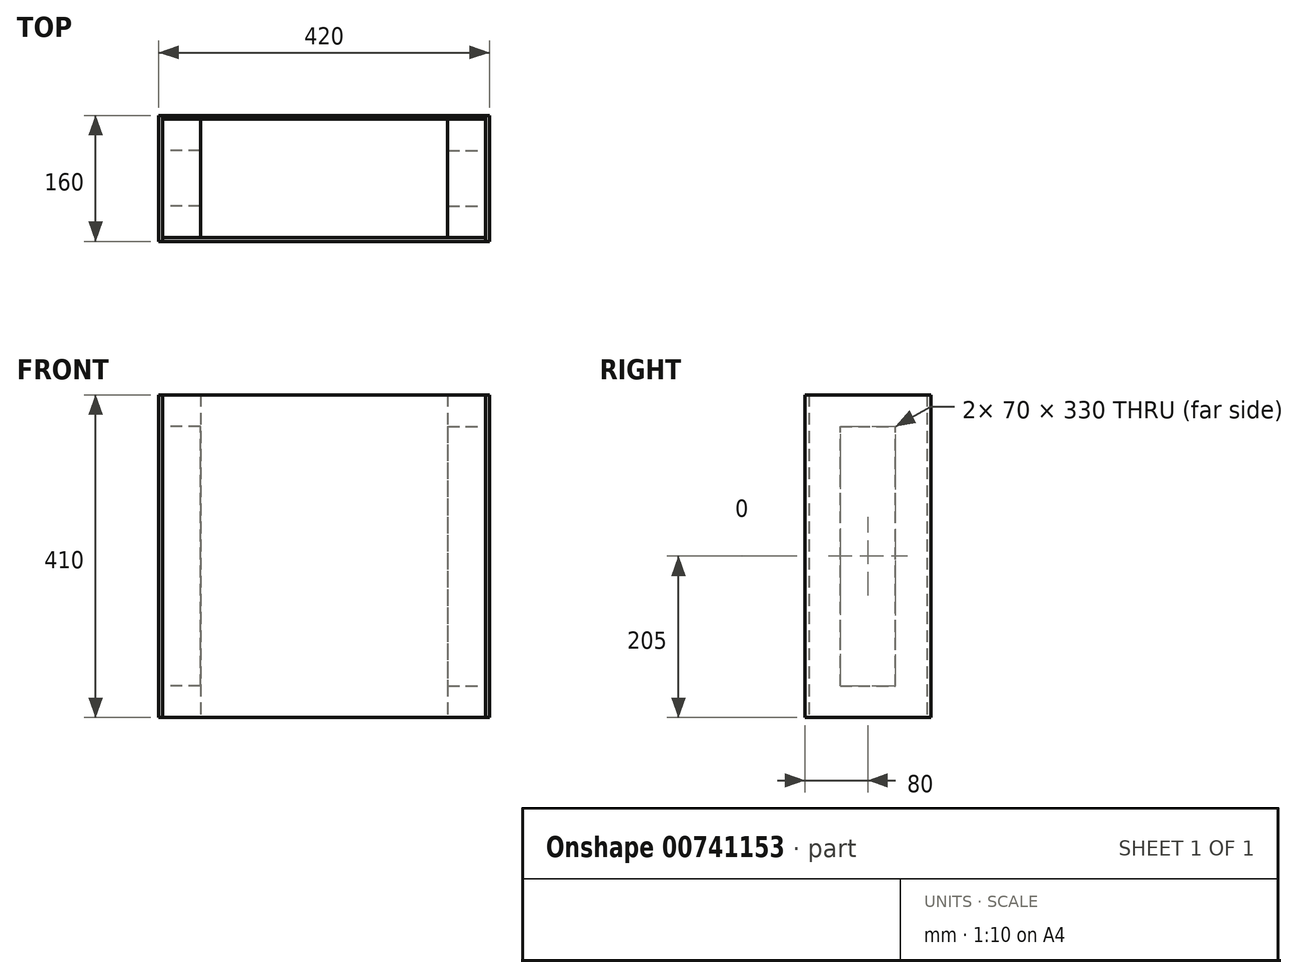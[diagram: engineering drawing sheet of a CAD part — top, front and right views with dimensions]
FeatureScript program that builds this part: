
annotation { "Feature Type Name" : "Feature", "Feature Type Description" : "" }
export const myFeature = defineFeature(function(context is Context, id is Id, definition is map)
    precondition{}
    {
        {
            var Q0;
            Q0=qCreatedBy(makeId("Front.planeOp"),FACE);
            var sketch = newSketch(context, id + "F0", { "sketchPlane" : qUnion([Q0])});
            skLineSegment(sketch, "E0.bottom", {"start": v(-205, 205) * mm, "end": v(205, 205) * mm});
            skLineSegment(sketch, "E0.top", {"start": v(-205, -205) * mm, "end": v(205, -205) * mm});
            skLineSegment(sketch, "E0.left", {"start": v(-205, 205) * mm, "end": v(-205, -205) * mm});
            skLineSegment(sketch, "E0.right", {"start": v(205, 205) * mm, "end": v(205, -205) * mm});
            skPoint(sketch, "E0.middle", {"position": v(0, 0) * mm});
            skSolve(sketch);
        }
        {
            var Q0;
            Q0 = qSketchRegion(id + "F0", true);
            extrude(context, id + "F1", {"entities" : qUnion([Q0]), "depth" : 5 * mm, "offsetDistance" : 25 * mm});
        }
        {
            var Q0;
            Q0=makeQuery(id+"F1.opExtrude","CAP_FACE",FACE,{"disambiguationData":[OSD([sQuery(id+"F0.wireOp",EDGE,"E0.bottom"),sQuery(id+"F0.wireOp",EDGE,"E0.top"),sQuery(id+"F0.wireOp",EDGE,"E0.left"),sQuery(id+"F0.wireOp",EDGE,"E0.right")])],"isStart":false});
            var sketch = newSketch(context, id + "F2", { "sketchPlane" : qUnion([Q0])});
            skLineSegment(sketch, "E1.0", {"start": v(-205, 205) * mm, "end": v(-205, -205) * mm});
            skLineSegment(sketch, "E2.0", {"start": v(205, 205) * mm, "end": v(205, -205) * mm});
            skLineSegment(sketch, "E3", {"start": v(0, 0) * mm, "end": v(0, 153.6) * mm, "construction": true});
            skLineSegment(sketch, "E4.bottom", {"start": v(-205, 205) * mm, "end": v(-157, 205) * mm});
            skLineSegment(sketch, "E4.top", {"start": v(-205, -205) * mm, "end": v(-157, -205) * mm});
            skLineSegment(sketch, "E4.right", {"start": v(-157, 205) * mm, "end": v(-157, -205) * mm});
            skLineSegment(sketch, "E5.MirrorCS", {"start": v(157, 205) * mm, "end": v(157, -205) * mm});
            skLineSegment(sketch, "E6.MirrorCS", {"start": v(205, 205) * mm, "end": v(157, 205) * mm});
            skLineSegment(sketch, "E7.MirrorCS", {"start": v(205, -205) * mm, "end": v(157, -205) * mm});
            skSolve(sketch);
        }
        {
            var Q0;
            Q0 = qSketchRegion(id + "F2", true);
            extrude(context, id + "F3", {"entities" : qUnion([Q0]), "depth" : 150 * mm, "offsetDistance" : 25 * mm});
        }
        {
            var Q0;
            Q0=makeQuery(id+"F3.opExtrude","CAP_FACE",FACE,{"disambiguationData":[OSD([sQuery(id+"F2.wireOp",EDGE,"E4.bottom"),sQuery(id+"F2.wireOp",EDGE,"E4.top"),sQuery(id+"F2.wireOp",EDGE,"E1.0"),sQuery(id+"F2.wireOp",EDGE,"E4.right")])],"isStart":false});
            var sketch = newSketch(context, id + "F4", { "sketchPlane" : qUnion([Q0])});
            skLineSegment(sketch, "E8.0", {"start": v(-205, 205) * mm, "end": v(-205, -205) * mm});
            skLineSegment(sketch, "E9.0", {"start": v(-205, 205) * mm, "end": v(205, 205) * mm});
            skLineSegment(sketch, "E10.0", {"start": v(205, 205) * mm, "end": v(205, -205) * mm});
            skLineSegment(sketch, "E11.0", {"start": v(-205, -205) * mm, "end": v(205, -205) * mm});
            skSolve(sketch);
        }
        {
            var Q0;
            Q0 = qSketchRegion(id + "F4", true);
            extrude(context, id + "F5", {"entities" : qUnion([Q0]), "depth" : 5 * mm, "offsetDistance" : 25 * mm});
        }
        {
            var Q0;
            Q0=makeQuery(id+"F3.opExtrude","SWEPT_FACE",FACE,{"disambiguationData":[OSD([sQuery(id+"F2.wireOp",EDGE,"E1.0")])]});
            var sketch = newSketch(context, id + "F6", { "sketchPlane" : qUnion([Q0])});
            skLineSegment(sketch, "E12.0", {"start": v(0, 205) * mm, "end": v(0, -205) * mm});
            skLineSegment(sketch, "E13.0", {"start": v(160, 205) * mm, "end": v(160, -205) * mm});
            skPoint(sketch, "E14.0.end.orphan", {"position": v(5, 205) * mm});
            skPoint(sketch, "E14.0.start.orphan", {"position": v(155, 205) * mm});
            skLineSegment(sketch, "E15", {"start": v(0, 205) * mm, "end": v(160, 205) * mm});
            skPoint(sketch, "E16.0.end.orphan", {"position": v(5, -205) * mm});
            skPoint(sketch, "E16.0.start.orphan", {"position": v(155, -205) * mm});
            skLineSegment(sketch, "E17", {"start": v(0, -205) * mm, "end": v(160, -205) * mm});
            skSolve(sketch);
        }
        {
            var Q0;
            Q0 = qSketchRegion(id + "F6", true);
            extrude(context, id + "F7", {"entities" : qUnion([Q0]), "depth" : 5 * mm, "offsetDistance" : 25 * mm});
        }
        {
            var Q0;
            Q0=makeQuery(id+"F3.opExtrude","SWEPT_FACE",FACE,{"disambiguationData":[OSD([sQuery(id+"F2.wireOp",EDGE,"E2.0")])]});
            var sketch = newSketch(context, id + "F8", { "sketchPlane" : qUnion([Q0])});
            skLineSegment(sketch, "E18.0", {"start": v(-160, 205) * mm, "end": v(-160, -205) * mm});
            skLineSegment(sketch, "E19.0", {"start": v(0, 205) * mm, "end": v(0, -205) * mm});
            skLineSegment(sketch, "E20", {"start": v(-160, 205) * mm, "end": v(0, 205) * mm});
            skLineSegment(sketch, "E21", {"start": v(-160, -205) * mm, "end": v(0, -205) * mm});
            skSolve(sketch);
        }
        {
            var Q0;
            Q0 = qSketchRegion(id + "F8", true);
            extrude(context, id + "F9", {"entities" : qUnion([Q0]), "depth" : 5 * mm, "offsetDistance" : 25 * mm});
        }
        {
            var Q0;
            Q0=makeQuery(id+"F3.opExtrude","SWEPT_FACE",FACE,{"disambiguationData":[OSD([sQuery(id+"F2.wireOp",EDGE,"E1.0")])]});
            var sketch = newSketch(context, id + "F10", { "sketchPlane" : qUnion([Q0])});
            skLineSegment(sketch, "E22.0", {"start": v(155, 205) * mm, "end": v(5, 205) * mm, "construction": true});
            skLineSegment(sketch, "E23.0", {"start": v(5, 205) * mm, "end": v(5, -205) * mm, "construction": true});
            skLineSegment(sketch, "E24.bottom", {"start": v(45, 165) * mm, "end": v(115, 165) * mm});
            skLineSegment(sketch, "E24.top", {"start": v(45, -165) * mm, "end": v(115, -165) * mm});
            skLineSegment(sketch, "E24.left", {"start": v(45, 165) * mm, "end": v(45, -165) * mm});
            skLineSegment(sketch, "E24.right", {"start": v(115, 165) * mm, "end": v(115, -165) * mm});
            skPoint(sketch, "E24.middle", {"position": v(80, 0) * mm});
            skPoint(sketch, "E24.middle.positionSnap0", {"position": v(80, 205) * mm});
            skPoint(sketch, "E24.centerSnap0", {"position": v(80, 205) * mm});
            skSolve(sketch);
        }
        {
            var Q0;
            Q0 = qSketchRegion(id + "F10", true);
            extrude(context, id + "F11", {"entities" : qUnion([Q0]), "operationType" : NewBodyOperationType.REMOVE, "oppositeDirection" : true, "depth" : 50 * mm, "offsetDistance" : 25 * mm});
        }
        {
            var Q0;
            Q0=makeQuery(id+"F3.opExtrude","SWEPT_FACE",FACE,{"disambiguationData":[OSD([sQuery(id+"F2.wireOp",EDGE,"E2.0")])]});
            var sketch = newSketch(context, id + "F12", { "sketchPlane" : qUnion([Q0])});
            skLineSegment(sketch, "E25.0", {"start": v(-45, 165) * mm, "end": v(-115, 165) * mm});
            skLineSegment(sketch, "E26.0", {"start": v(-115, 165) * mm, "end": v(-115, -165) * mm});
            skLineSegment(sketch, "E27.0", {"start": v(-45, 165) * mm, "end": v(-45, -165) * mm});
            skLineSegment(sketch, "E28.0", {"start": v(-45, -165) * mm, "end": v(-115, -165) * mm});
            skSolve(sketch);
        }
        {
            var Q0;
            Q0 = qSketchRegion(id + "F12", true);
            extrude(context, id + "F13", {"entities" : qUnion([Q0]), "operationType" : NewBodyOperationType.REMOVE, "oppositeDirection" : true, "depth" : 50 * mm, "offsetDistance" : 25 * mm});
        }
    });
